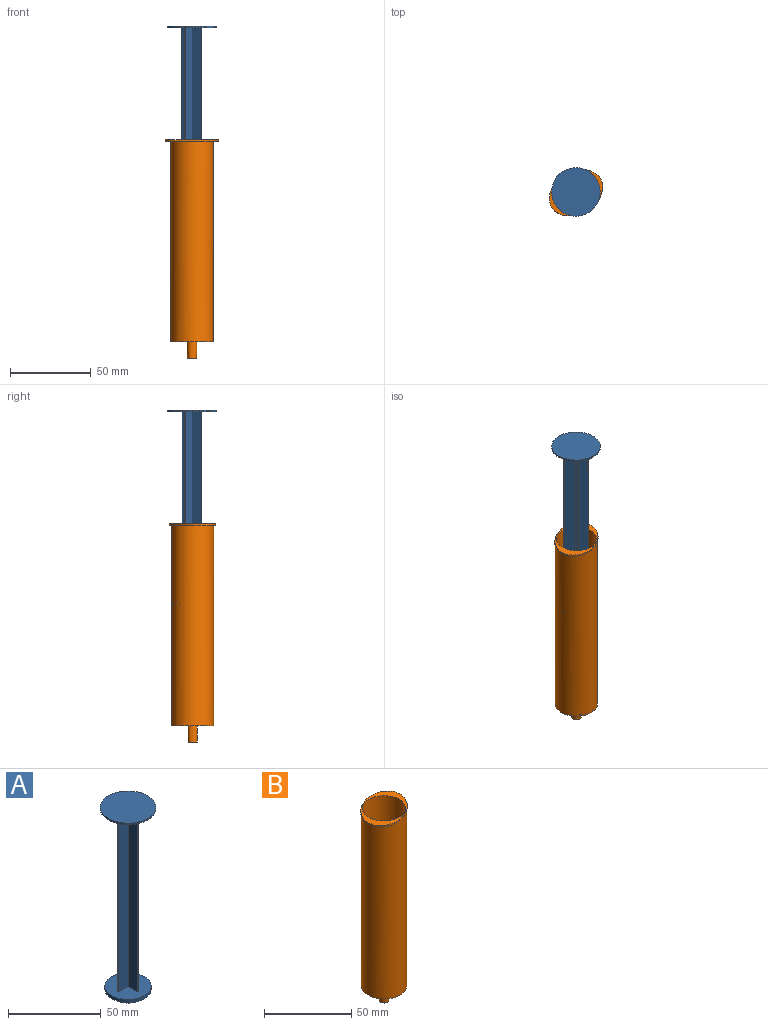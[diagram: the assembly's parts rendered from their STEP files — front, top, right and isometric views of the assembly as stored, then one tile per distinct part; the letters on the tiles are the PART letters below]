
ASSEMBLY  parts=2 mates=1
PART A: 19 faces, bbox 30x30x122 mm
  f0: cylinder r=15mm len=30mm, axis (0,0,-1), area 94.2mm2, adj f1,f2
  f1: plane 30x30mm, normal (0,0,1), area 706.9mm2, adj f0
  f2: plane 30x30mm, normal (0,0,-1), area 692.1mm2, adj f0,f3,f4,f5,f6,f7,f8,f9
  f3: plane 117x0.5mm, normal (0,1,0), area 58.5mm2, adj f2,f4,f14,f15
  f4: plane 117x7.25mm, normal (1,0,0), area 848.2mm2, adj f2,f3,f5,f15
  f5: plane 117x7.25mm, normal (0,1,0), area 848.2mm2, adj f2,f4,f6,f15
  f6: plane 117x0.5mm, normal (1,0,0), area 58.5mm2, adj f2,f5,f7,f15
  f7: plane 117x7.25mm, normal (0,-1,0), area 848.2mm2, adj f2,f6,f8,f15
  f8: plane 117x7.25mm, normal (1,0,0), area 848.3mm2, adj f2,f7,f9,f15
  f9: plane 117x0.5mm, normal (0,-1,0), area 58.5mm2, adj f2,f8,f10,f15
  f10: plane 117x7.25mm, normal (-1,0,0), area 848.3mm2, adj f2,f9,f11,f15
  f11: plane 117x7.25mm, normal (0,-1,0), area 848.2mm2, adj f2,f10,f12,f15
  f12: plane 117x0.5mm, normal (-1,0,0), area 58.5mm2, adj f2,f11,f13,f15
  f13: plane 117x7.25mm, normal (0,1,0), area 848.2mm2, adj f2,f12,f14,f15
  f14: plane 117x7.25mm, normal (-1,0,0), area 848.2mm2, adj f2,f3,f13,f15
  f15: plane 25x25mm, normal (0,0,1), area 476.1mm2, adj f3,f4,f5,f6,f7,f8,f9,f10
  f16: cone r=12.5mm half-angle=50deg, axis (0,0,1), area 221.1mm2, adj f17,f18
  f17: plane 20.23x20.23mm, normal (0,0,-1), area 321.5mm2, adj f16
  f18: cylinder r=12.5mm len=25mm, axis (0,0,1), area 157.1mm2, adj f15,f16
PART B: 14 faces, bbox 33x28.5x135 mm
  f0: cylinder r=13mm len=124mm, axis (0,0,-1), area 10128.5mm2, adj f3,f5,f6
  f1: cylinder r=12.5mm len=124mm, axis (0,0,-1), area 9738.9mm2, adj f2,f8
  f2: plane 32.96x28.54mm, normal (0,0,1), area 223.8mm2, adj f1,f4
  f3: plane 26x26mm, normal (0,0,-1), area 502.7mm2, adj f0,f12
  f4: extruded ~32.96x28.46mm, area 96.3mm2, adj f2,f5,f6
  f5: plane 25.51x23.01mm, normal (0,0,-1), area 91.9mm2, adj f0,f4
  f6: plane 25.51x23.01mm, normal (0,0,-1), area 91.9mm2, adj f0,f4
  f7: cylinder r=3mm len=6mm, axis (0,0,-1), area 9.4mm2, adj f8,f10
  f8: plane 25x25mm, normal (0,0,1), area 462.6mm2, adj f1,f7
  f9: cylinder r=2.5mm len=5mm, axis (0,0,-1), area 7.9mm2, adj f10,f11
  f10: plane 6x6mm, normal (0,0,1), area 8.6mm2, adj f7,f9
  f11: cone r=2.5mm half-angle=1deg, axis (0,0,-1), area 162.6mm2, adj f9,f13
  f12: cone r=3mm half-angle=1deg, axis (0,0,1), area 183mm2, adj f3,f13
  f13: plane 5.65x5.65mm, normal (0,0,-1), area 2.6mm2, adj f11,f12
PLACE A rot(axis=(0,0,1),53.4deg) t=(-18.12,-36.2,9.86)mm
PLACE B t=(-0.27,0.04,-65.29)mm fixed
MATE cylindrical B.f1 <-> A.f15  axis (0,0,-1) through (-0.27,0.04,-2.29)mm
